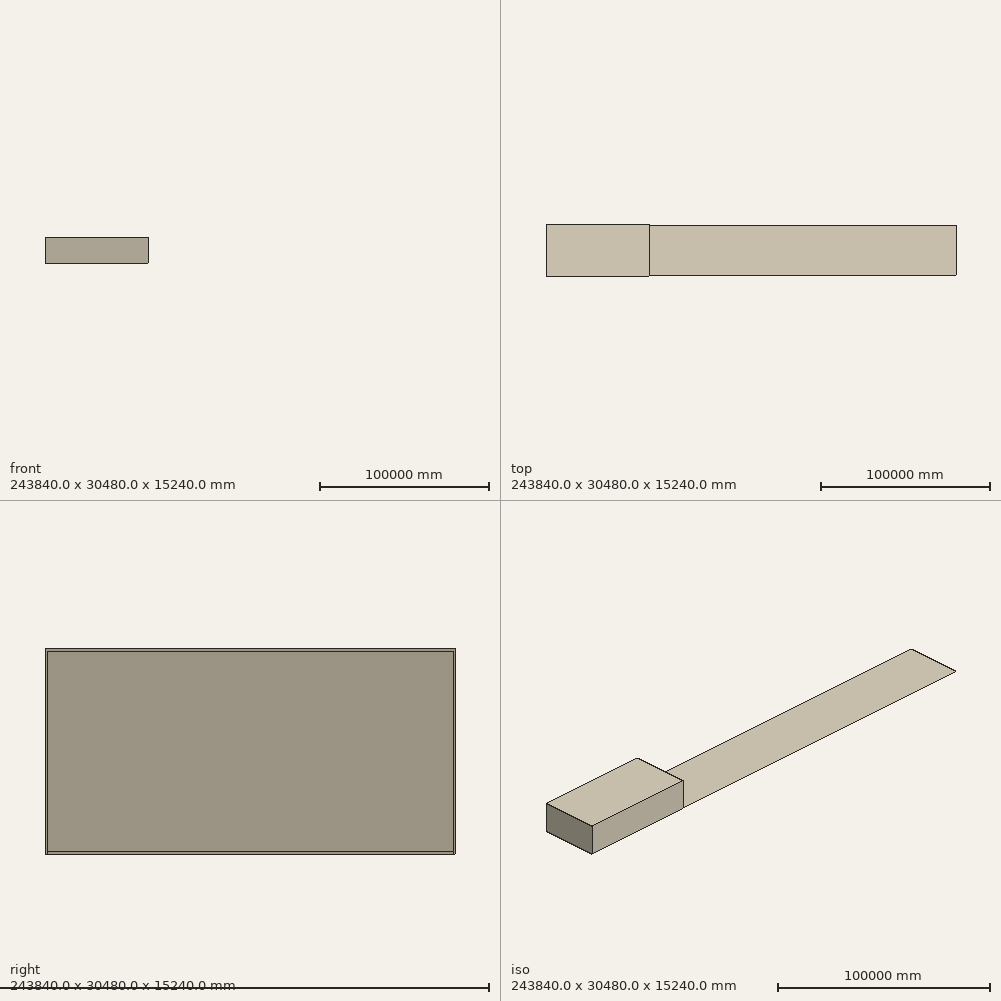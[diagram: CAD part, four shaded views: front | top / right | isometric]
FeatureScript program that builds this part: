
annotation { "Feature Type Name" : "Feature", "Feature Type Description" : "" }
export const myFeature = defineFeature(function(context is Context, id is Id, definition is map)
    precondition{}
    {
        {
            var Q0;
            Q0=qCreatedBy(makeId("Top.planeOp"),FACE);
            var sketch = newSketch(context, id + "F0", { "sketchPlane" : qUnion([Q0])});
            skLineSegment(sketch, "E0.bottom", {"start": v(30480, 15240) * mm, "end": v(-30480, 15240) * mm});
            skLineSegment(sketch, "E0.top", {"start": v(30480, -15240) * mm, "end": v(-30480, -15240) * mm});
            skLineSegment(sketch, "E0.left", {"start": v(30480, 15240) * mm, "end": v(30480, -15240) * mm});
            skLineSegment(sketch, "E0.right", {"start": v(-30480, 15240) * mm, "end": v(-30480, -15240) * mm});
            skPoint(sketch, "E0.middle", {"position": v(0, 0) * mm});
            skSolve(sketch);
        }
        {
            var Q0;
            Q0=makeQuery(id+"F0.imprint","IMPRINT",FACE,{"disambiguationData":[TD([[makeQuery(id+"F0.imprint","IMPRINT",EDGE,{"derivedFrom":sQuery(id+"F0.wireOp",EDGE,"E0.bottom")}),1.0]])]});
            extrude(context, id + "F1", {"entities" : qUnion([Q0]), "depth" : 15240 * mm, "offsetDistance" : 25.4 * mm});
        }
        {
            var Q0;
            Q0=makeQuery(id+"F1.opExtrude","SWEPT_FACE",FACE,{"disambiguationData":[OSD([sQuery(id+"F0.wireOp",EDGE,"E0.left")])]});
            shell(context, id + "F2", {"entities" : qUnion([Q0]), "thickness" : 152.4 * mm});
        }
        {
            var Q0;
            Q0=makeQuery(id+"F1.opExtrude","SWEPT_FACE",FACE,{"disambiguationData":[OSD([sQuery(id+"F0.wireOp",EDGE,"E0.left")])]});
            var sketch = newSketch(context, id + "F3", { "sketchPlane" : qUnion([Q0])});
            skLineSegment(sketch, "E1", {"start": v(15087.6, 152.4) * mm, "end": v(15087.6, 0) * mm});
            skLineSegment(sketch, "E2", {"start": v(-15087.6, 152.4) * mm, "end": v(-15087.6, 0) * mm});
            skSolve(sketch);
        }
        {
            var Q0;
            {var subQ0=sQuery(id+"F3.wireOp",EDGE,"E1");Q0=makeQuery(id+"F3.imprint","IMPRINT",FACE,{"disambiguationData":[TD([[makeQuery(id+"F3.imprint","IMPRINT",EDGE,{"derivedFrom":subQ0}),-1.0]])]});}
            extrude(context, id + "F4", {"entities" : qUnion([Q0]), "operationType" : NewBodyOperationType.ADD, "depth" : 182880 * mm, "offsetDistance" : 25.4 * mm});
        }
    });
